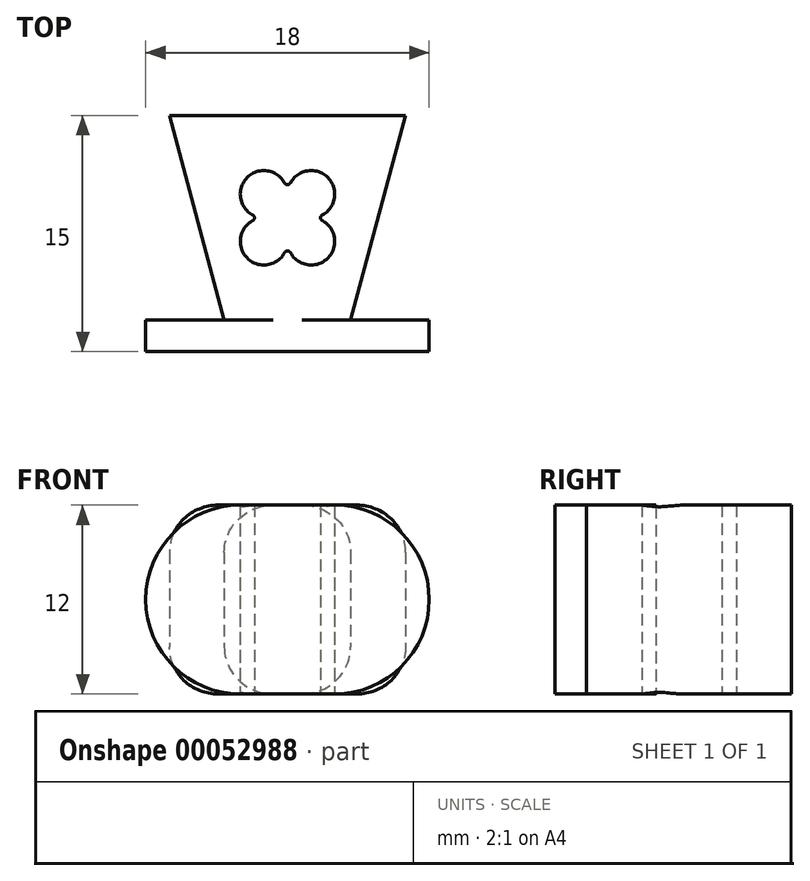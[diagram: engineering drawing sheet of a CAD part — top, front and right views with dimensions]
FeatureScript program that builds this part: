
annotation { "Feature Type Name" : "Feature", "Feature Type Description" : "" }
export const myFeature = defineFeature(function(context is Context, id is Id, definition is map)
    precondition{}
    {
        {
            var Q0;
            Q0=qCreatedBy(makeId("Top.planeOp"),FACE);
            var sketch = newSketch(context, id + "F0", { "sketchPlane" : qUnion([Q0])});
            skLineSegment(sketch, "E0.bottom", {"start": v(-9, -7) * mm, "end": v(9, -7) * mm});
            skLineSegment(sketch, "E0.left", {"start": v(-9, -7) * mm, "end": v(-9, -5) * mm});
            skLineSegment(sketch, "E0.right", {"start": v(9, -7) * mm, "end": v(9, -5) * mm});
            skLineSegment(sketch, "E1.top", {"start": v(7.5, 8) * mm, "end": v(-7.5, 8) * mm});
            skLineSegment(sketch, "E2", {"start": v(-9, -5) * mm, "end": v(9, -5) * mm});
            skLineSegment(sketch, "E3", {"start": v(-7.5, 8) * mm, "end": v(-4.02, -5) * mm});
            skLineSegment(sketch, "E4", {"start": v(0, 8) * mm, "end": v(0, -5) * mm, "construction": true});
            skLineSegment(sketch, "E5.MirrorCS", {"start": v(7.5, 8) * mm, "end": v(4.02, -5) * mm});
            skLineSegment(sketch, "E6.0", {"start": v(1.5, 0) * mm, "end": v(-1.5, 0) * mm, "construction": true});
            skLineSegment(sketch, "E6.1", {"start": v(-1.5, 0) * mm, "end": v(-1.5, 3) * mm, "construction": true});
            skLineSegment(sketch, "E6.2", {"start": v(-1.5, 3) * mm, "end": v(1.5, 3) * mm, "construction": true});
            skLineSegment(sketch, "E6.3", {"start": v(1.5, 3) * mm, "end": v(1.5, 0) * mm, "construction": true});
            skPoint(sketch, "E6.0.midPoint", {"position": v(0, 0) * mm});
            skArc(sketch, "E7", {"start": v(0, 3) * mm, "mid": v(-2.56, 4.06) * mm, "end": v(-1.5, 1.5) * mm});
            skArc(sketch, "E8", {"start": v(1.5, 1.5) * mm, "mid": v(2.56, 4.06) * mm, "end": v(0, 3) * mm});
            skArc(sketch, "E9", {"start": v(0, 0) * mm, "mid": v(2.56, -1.06) * mm, "end": v(1.5, 1.5) * mm});
            skArc(sketch, "E10", {"start": v(-1.5, 1.5) * mm, "mid": v(-2.56, -1.06) * mm, "end": v(0, 0) * mm});
            skLineSegment(sketch, "E11", {"start": v(-4.42, -3.5) * mm, "end": v(4.42, -3.5) * mm});
            skSolve(sketch);
        }
        {
            var Q0;
            {var subQ1=sQuery(id+"F0.wireOp",EDGE,"E1.top");Q0=makeQuery(id+"F0.imprint","IMPRINT",FACE,{"disambiguationData":[TD([[makeQuery(id+"F0.imprint","IMPRINT",EDGE,{"derivedFrom":subQ1}),1.0]])]});}
            var Q1;
            Q1=makeQuery(id+"F0.imprint","IMPRINT",FACE,{"disambiguationData":[TD([[makeQuery(id+"F0.imprint","IMPRINT",EDGE,{"derivedFrom":sQuery(id+"F0.wireOp",EDGE,"E0.bottom")}),1.0]])]});
            var Q2;
            {var subQ5=sQuery(id+"F0.wireOp",EDGE,"E11");Q2=makeQuery(id+"F0.imprint","IMPRINT",FACE,{"disambiguationData":[TD([[makeQuery(id+"F0.imprint","IMPRINT",EDGE,{"derivedFrom":subQ5}),-1.0]])]});}
            extrude(context, id + "F1", {"entities" : qUnion([Q0, Q1, Q2]), "depth" : 6 * mm});
        }
        {
            var Q0;
            Q0=makeQuery(id+"F1.opExtrude","SWEPT_EDGE",EDGE,{"disambiguationData":[OSD([sQuery(id+"F0.wireOp",EDGE,"E7"),sQuery(id+"F0.wireOp",EDGE,"E10")])]});
            var Q1;
            Q1=makeQuery(id+"F1.opExtrude","SWEPT_EDGE",EDGE,{"disambiguationData":[OSD([sQuery(id+"F0.wireOp",EDGE,"E7"),sQuery(id+"F0.wireOp",EDGE,"E8")])]});
            var Q2;
            Q2=makeQuery(id+"F1.opExtrude","SWEPT_EDGE",EDGE,{"disambiguationData":[OSD([sQuery(id+"F0.wireOp",EDGE,"E8"),sQuery(id+"F0.wireOp",EDGE,"E9")])]});
            var Q3;
            Q3=makeQuery(id+"F1.opExtrude","SWEPT_EDGE",EDGE,{"disambiguationData":[OSD([sQuery(id+"F0.wireOp",EDGE,"E9"),sQuery(id+"F0.wireOp",EDGE,"E10")])]});
            fillet(context, id + "F2", {"entities" : qUnion([Q0, Q1, Q2, Q3]), "radius" : 0.2 * mm, "tangentPropagation" : true, "allowEdgeOverflow" : false});
        }
        {
            var Q0;
            Q0=makeQuery(id+"F1.opExtrude","CAP_EDGE",EDGE,{"disambiguationData":[OSD([sQuery(id+"F0.wireOp",EDGE,"E3")])],"isStart":false});
            var Q1;
            Q1=makeQuery(id+"F1.opExtrude","CAP_EDGE",EDGE,{"disambiguationData":[OSD([sQuery(id+"F0.wireOp",EDGE,"E5.MirrorCS")])],"isStart":false});
            fillet(context, id + "F3", {"entities" : qUnion([Q0, Q1]), "radius" : 3 * mm, "tangentPropagation" : true, "allowEdgeOverflow" : false});
        }
        {
            var Q0;
            Q0=makeQuery(id+"F1.opExtrude","CAP_EDGE",EDGE,{"disambiguationData":[OSD([sQuery(id+"F0.wireOp",EDGE,"E0.right")])],"isStart":false});
            var Q1;
            Q1=makeQuery(id+"F1.opExtrude","CAP_EDGE",EDGE,{"disambiguationData":[OSD([sQuery(id+"F0.wireOp",EDGE,"E0.left")])],"isStart":false});
            fillet(context, id + "F4", {"entities" : qUnion([Q0, Q1]), "radius" : 6 * mm, "tangentPropagation" : true, "allowEdgeOverflow" : false});
        }
        {
            var Q0;
            Q0=makeQuery(id+"F1.opExtrude","SWEPT_BODY",BODY,{"disambiguationData":[OSD([sQuery(id+"F0.wireOp",EDGE,"E0.bottom"),sQuery(id+"F0.wireOp",EDGE,"E0.left"),sQuery(id+"F0.wireOp",EDGE,"E0.right"),sQuery(id+"F0.wireOp",EDGE,"E1.top"),sQuery(id+"F0.wireOp",EDGE,"E2"),sQuery(id+"F0.wireOp",EDGE,"E3"),sQuery(id+"F0.wireOp",EDGE,"E5.MirrorCS"),sQuery(id+"F0.wireOp",EDGE,"E7"),sQuery(id+"F0.wireOp",EDGE,"E8"),sQuery(id+"F0.wireOp",EDGE,"E9"),sQuery(id+"F0.wireOp",EDGE,"E10")])]});
            var Q1;
            Q1=qCreatedBy(makeId("Top.planeOp"),FACE);
            mirror(context, id + "F5", {"operationType" : NewBodyOperationType.ADD, "entities" : qUnion([Q0]), "mirrorPlane" : qUnion([Q1])});
        }
    });
